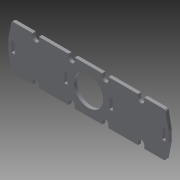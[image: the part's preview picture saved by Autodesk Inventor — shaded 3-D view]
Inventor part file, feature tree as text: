
AUTODESK INVENTOR PART (.ipt)
format: ipt  version: 2015 (Build 190159000, 159)  size: 192,512 bytes
history: native  units: mm
features: extrude x1, sketch x1
ambient origin geometry x8: Origin, YZ Plane, XZ Plane, XY Plane, X Axis, Y Axis, Z Axis, Center Point
bodies: Solid1 (feature_tree)
feature tree (2):
  extrude  "Extrusion1"  Depth=28.0mm
  sketch  "Sketch1"  dims[d2=42.0mm d3=28.0mm d4=76.0mm d5=21.0mm d6=3.0mm d7=10.0mm d8=20.0mm d9=3.0mm d10=10.0mm d11=20.0mm d12=3.0mm d13=10.0mm d14=3.0mm d15=3.0mm d16=10.0mm d17=3.0mm d18=5.0mm d19=5.0mm d20=6.0mm d21=16.0mm d22=3.0mm d23=3.0mm d24=6.0mm d25=16.0mm d26=6.0mm d27=16.0mm d28=6.0mm d29=16.0mm d30=3.0mm d31=3.0mm d32=6.0mm d33=50.0mm d34=3.0mm d35=50.0mm d36=3.0mm d37=0.0mm d38=76.0mm d39=21.0mm d40=3.0mm d41=3.0mm d42=10.0mm d43=10.0mm d44=21.0mm d45=2.0mm d46=50.0mm d47=50.0mm d48=3.0mm d49=3.0mm d50=3.0mm d51=3.0mm d52=3.0mm d53=3.0mm d54=3.0mm d55=3.0mm d56=17.561443mm]
